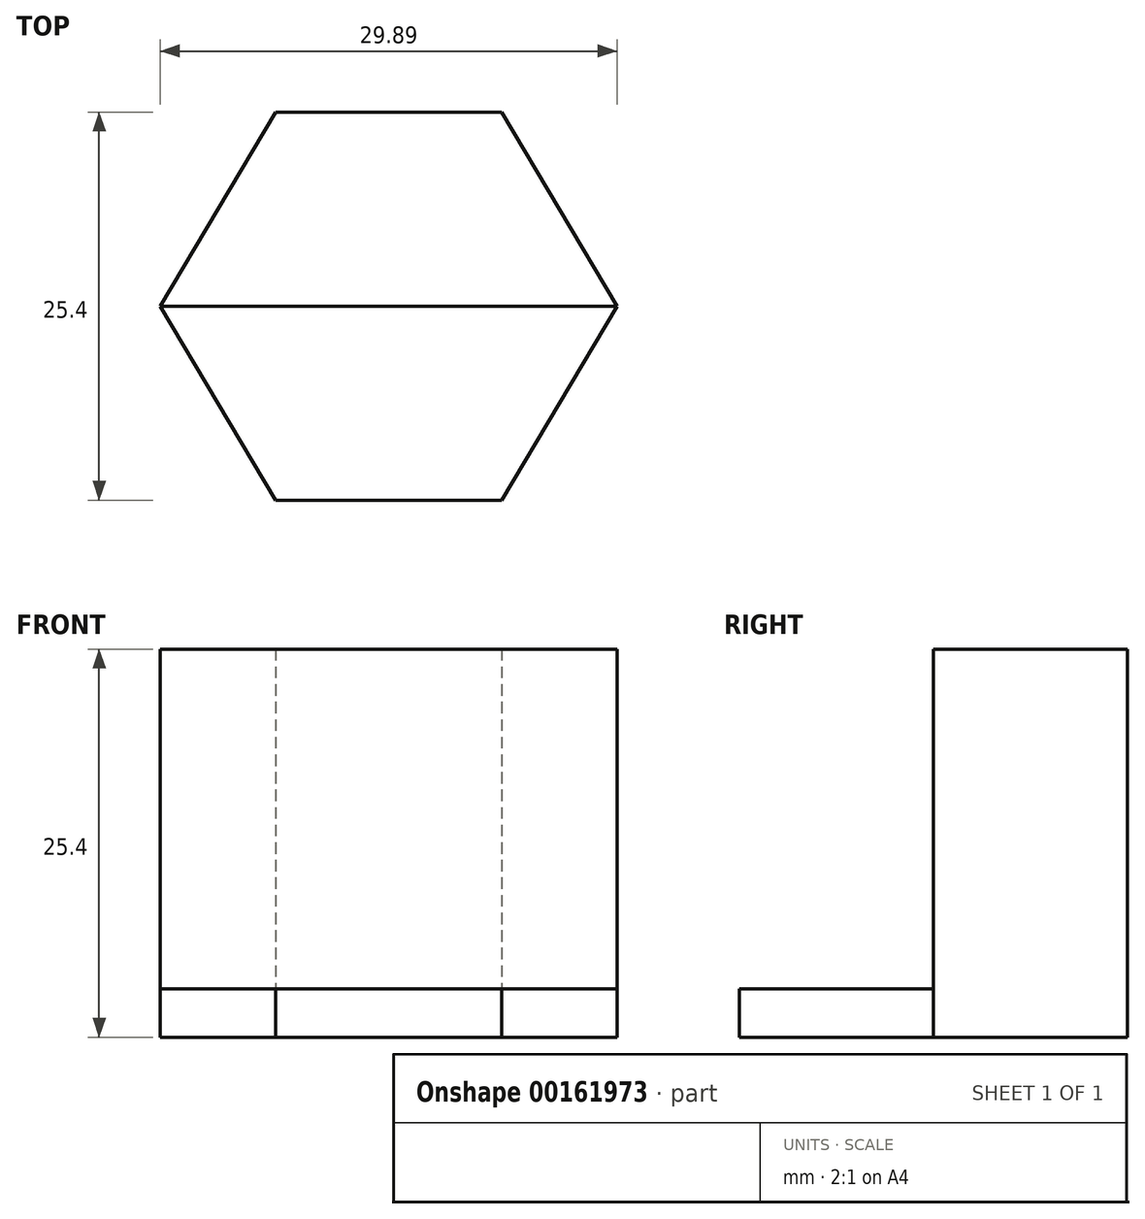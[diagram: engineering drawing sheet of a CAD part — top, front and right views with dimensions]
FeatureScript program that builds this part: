
annotation { "Feature Type Name" : "Feature", "Feature Type Description" : "" }
export const myFeature = defineFeature(function(context is Context, id is Id, definition is map)
    precondition{}
    {
        {
            var Q0;
            Q0=qCreatedBy(makeId("Top.planeOp"),FACE);
            var sketch = newSketch(context, id + "F0", { "sketchPlane" : qUnion([Q0])});
            skLineSegment(sketch, "E0", {"start": v(0, 0) * mm, "end": v(7.56, 12.7) * mm});
            skLineSegment(sketch, "E1", {"start": v(7.56, 12.7) * mm, "end": v(22.34, 12.7) * mm});
            skLineSegment(sketch, "E2", {"start": v(22.34, 12.7) * mm, "end": v(29.9, 0) * mm});
            skLineSegment(sketch, "E3", {"start": v(29.9, 0) * mm, "end": v(22.34, -12.7) * mm});
            skLineSegment(sketch, "E4", {"start": v(22.34, -12.7) * mm, "end": v(7.56, -12.7) * mm});
            skLineSegment(sketch, "E5", {"start": v(7.56, -12.7) * mm, "end": v(0, 0) * mm});
            skSolve(sketch);
        }
        {
            var Q0;
            Q0=makeQuery(id+"F0.imprint","IMPRINT",FACE,{"disambiguationData":[TD([[makeQuery(id+"F0.imprint","IMPRINT",EDGE,{"derivedFrom":sQuery(id+"F0.wireOp",EDGE,"E0")}),-1.0]])]});
            extrude(context, id + "F1", {"entities" : qUnion([Q0]), "depth" : 3.17 * mm});
        }
        {
            var Q0;
            Q0=makeQuery(id+"F1.opExtrude","CAP_FACE",FACE,{"disambiguationData":[OSD([sQuery(id+"F0.wireOp",EDGE,"E0"),sQuery(id+"F0.wireOp",EDGE,"E1"),sQuery(id+"F0.wireOp",EDGE,"E2"),sQuery(id+"F0.wireOp",EDGE,"E3"),sQuery(id+"F0.wireOp",EDGE,"E4"),sQuery(id+"F0.wireOp",EDGE,"E5")])],"isStart":false});
            var sketch = newSketch(context, id + "F2", { "sketchPlane" : qUnion([Q0])});
            skLineSegment(sketch, "E6", {"start": v(0, 0) * mm, "end": v(29.9, 0) * mm});
            skSolve(sketch);
        }
        {
            var Q0;
            Q0 = qSketchRegion(id + "F2", true);
            var Q1;
            Q1=makeQuery(id+"F2.imprint","IMPRINT",FACE,{"disambiguationData":[TD([[makeQuery(id+"F2.imprint","IMPRINT",EDGE,{"derivedFrom":sQuery(id+"F2.wireOp",EDGE,"E6")}),1.0]])]});
            extrude(context, id + "F3", {"entities" : qUnion([Q0, Q1]), "operationType" : NewBodyOperationType.ADD, "depth" : 22.22 * mm});
        }
    });
